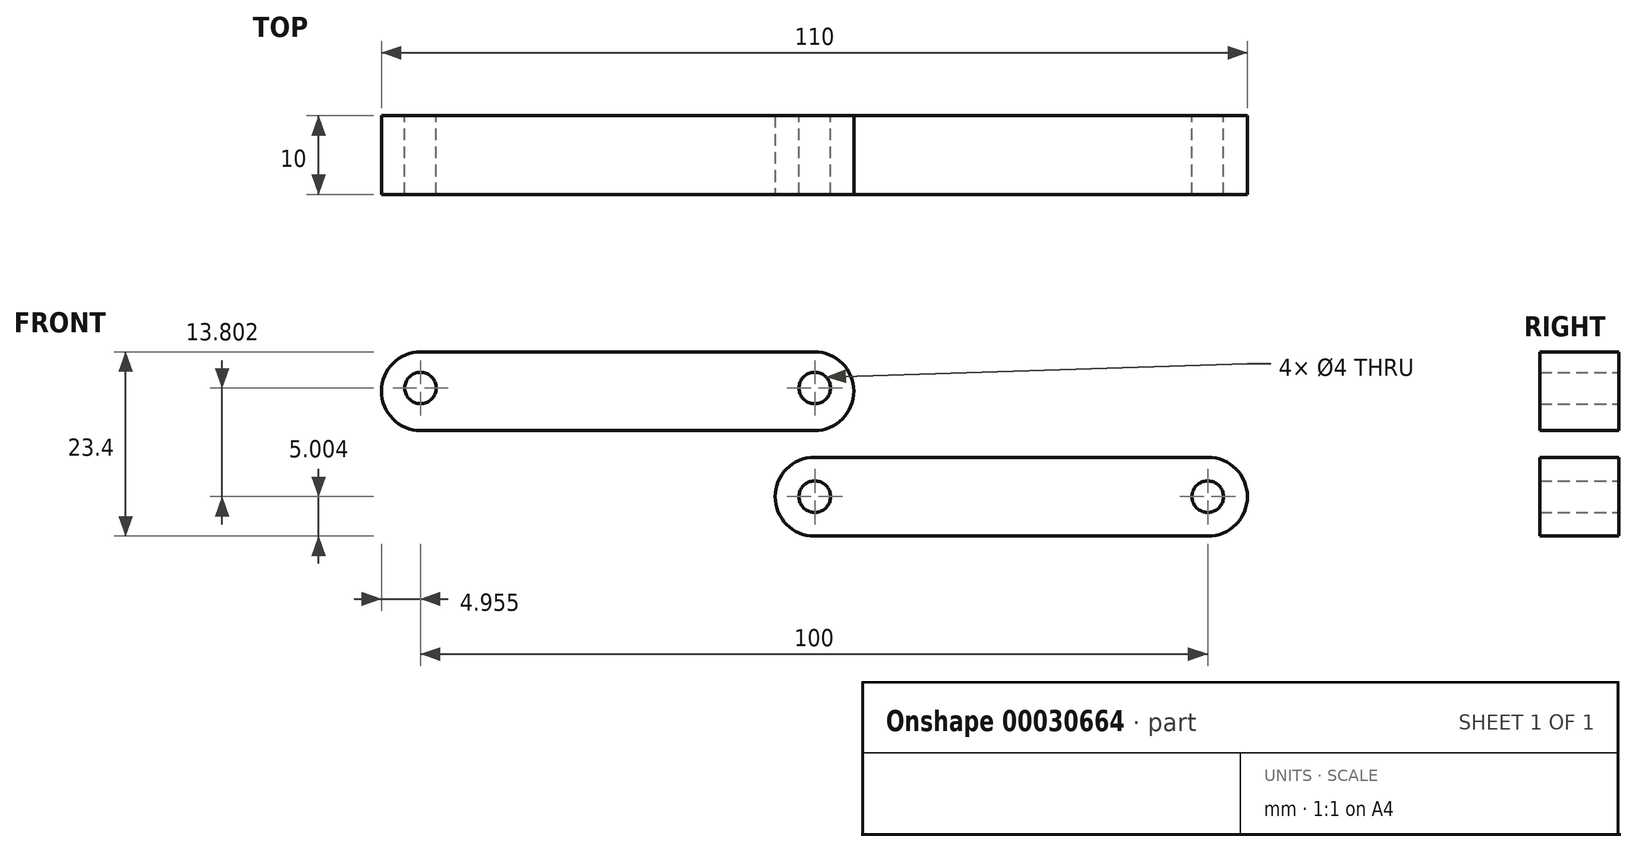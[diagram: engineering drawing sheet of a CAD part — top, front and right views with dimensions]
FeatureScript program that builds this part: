
annotation { "Feature Type Name" : "Feature", "Feature Type Description" : "" }
export const myFeature = defineFeature(function(context is Context, id is Id, definition is map)
    precondition{}
    {
        {
            var Q0;
            Q0=qCreatedBy(makeId("Front.planeOp"),FACE);
            var sketch = newSketch(context, id + "F0", { "sketchPlane" : qUnion([Q0])});
            skLineSegment(sketch, "E0.bottom", {"start": v(-817.4, -222.73) * mm, "end": v(-757.4, -222.73) * mm});
            skLineSegment(sketch, "E0.top", {"start": v(-817.4, -232.73) * mm, "end": v(-757.4, -232.73) * mm});
            skLineSegment(sketch, "E0.left", {"start": v(-817.4, -222.73) * mm, "end": v(-817.4, -232.73) * mm});
            skLineSegment(sketch, "E0.right", {"start": v(-757.4, -222.73) * mm, "end": v(-757.4, -232.73) * mm});
            skLineSegment(sketch, "E1.bottom", {"start": v(-767.4, -236.13) * mm, "end": v(-707.4, -236.13) * mm});
            skLineSegment(sketch, "E1.top", {"start": v(-767.4, -246.13) * mm, "end": v(-707.4, -246.13) * mm});
            skLineSegment(sketch, "E1.left", {"start": v(-767.4, -236.13) * mm, "end": v(-767.4, -246.13) * mm});
            skLineSegment(sketch, "E1.right", {"start": v(-707.4, -236.13) * mm, "end": v(-707.4, -246.13) * mm});
            skCircle(sketch, "E2", {"center": v(-762.36, -227.32) * mm, "radius": 2 * mm});
            skCircle(sketch, "E3", {"center": v(-762.36, -241.13) * mm, "radius": 2 * mm});
            skLineSegment(sketch, "E4", {"start": v(-737.4, -236.13) * mm, "end": v(-737.4, -246.13) * mm, "construction": true});
            skCircle(sketch, "E5.MirrorC", {"center": v(-712.44, -241.13) * mm, "radius": 2 * mm});
            skLineSegment(sketch, "E6", {"start": v(-787.4, -222.73) * mm, "end": v(-787.4, -232.73) * mm, "construction": true});
            skCircle(sketch, "E7.MirrorC", {"center": v(-812.44, -227.32) * mm, "radius": 2 * mm});
            skSolve(sketch);
        }
        {
            var Q0;
            Q0 = qSketchRegion(id + "F0", true);
            extrude(context, id + "F1", {"entities" : qUnion([Q0]), "depth" : 10 * mm});
        }
        {
            var Q0;
            Q0=makeQuery(id+"F1.opExtrude","SWEPT_EDGE",EDGE,{"disambiguationData":[OSD([sQuery(id+"F0.wireOp",EDGE,"E0.bottom"),sQuery(id+"F0.wireOp",EDGE,"E0.right")])]});
            var Q1;
            Q1=makeQuery(id+"F1.opExtrude","SWEPT_EDGE",EDGE,{"disambiguationData":[OSD([sQuery(id+"F0.wireOp",EDGE,"E0.top"),sQuery(id+"F0.wireOp",EDGE,"E0.right")])]});
            var Q2;
            Q2=makeQuery(id+"F1.opExtrude","SWEPT_EDGE",EDGE,{"disambiguationData":[OSD([sQuery(id+"F0.wireOp",EDGE,"E0.bottom"),sQuery(id+"F0.wireOp",EDGE,"E0.left")])]});
            var Q3;
            Q3=makeQuery(id+"F1.opExtrude","SWEPT_EDGE",EDGE,{"disambiguationData":[OSD([sQuery(id+"F0.wireOp",EDGE,"E0.top"),sQuery(id+"F0.wireOp",EDGE,"E0.left")])]});
            var Q4;
            Q4=makeQuery(id+"F1.opExtrude","SWEPT_EDGE",EDGE,{"disambiguationData":[OSD([sQuery(id+"F0.wireOp",EDGE,"E1.bottom"),sQuery(id+"F0.wireOp",EDGE,"E1.left")])]});
            var Q5;
            Q5=makeQuery(id+"F1.opExtrude","SWEPT_EDGE",EDGE,{"disambiguationData":[OSD([sQuery(id+"F0.wireOp",EDGE,"E1.top"),sQuery(id+"F0.wireOp",EDGE,"E1.left")])]});
            var Q6;
            Q6=makeQuery(id+"F1.opExtrude","SWEPT_EDGE",EDGE,{"disambiguationData":[OSD([sQuery(id+"F0.wireOp",EDGE,"E1.bottom"),sQuery(id+"F0.wireOp",EDGE,"E1.right")])]});
            var Q7;
            Q7=makeQuery(id+"F1.opExtrude","SWEPT_EDGE",EDGE,{"disambiguationData":[OSD([sQuery(id+"F0.wireOp",EDGE,"E1.top"),sQuery(id+"F0.wireOp",EDGE,"E1.right")])]});
            fillet(context, id + "F2", {"entities" : qUnion([Q0, Q1, Q2, Q3, Q4, Q5, Q6, Q7]), "radius" : 5 * mm, "tangentPropagation" : true, "allowEdgeOverflow" : false});
        }
    });
